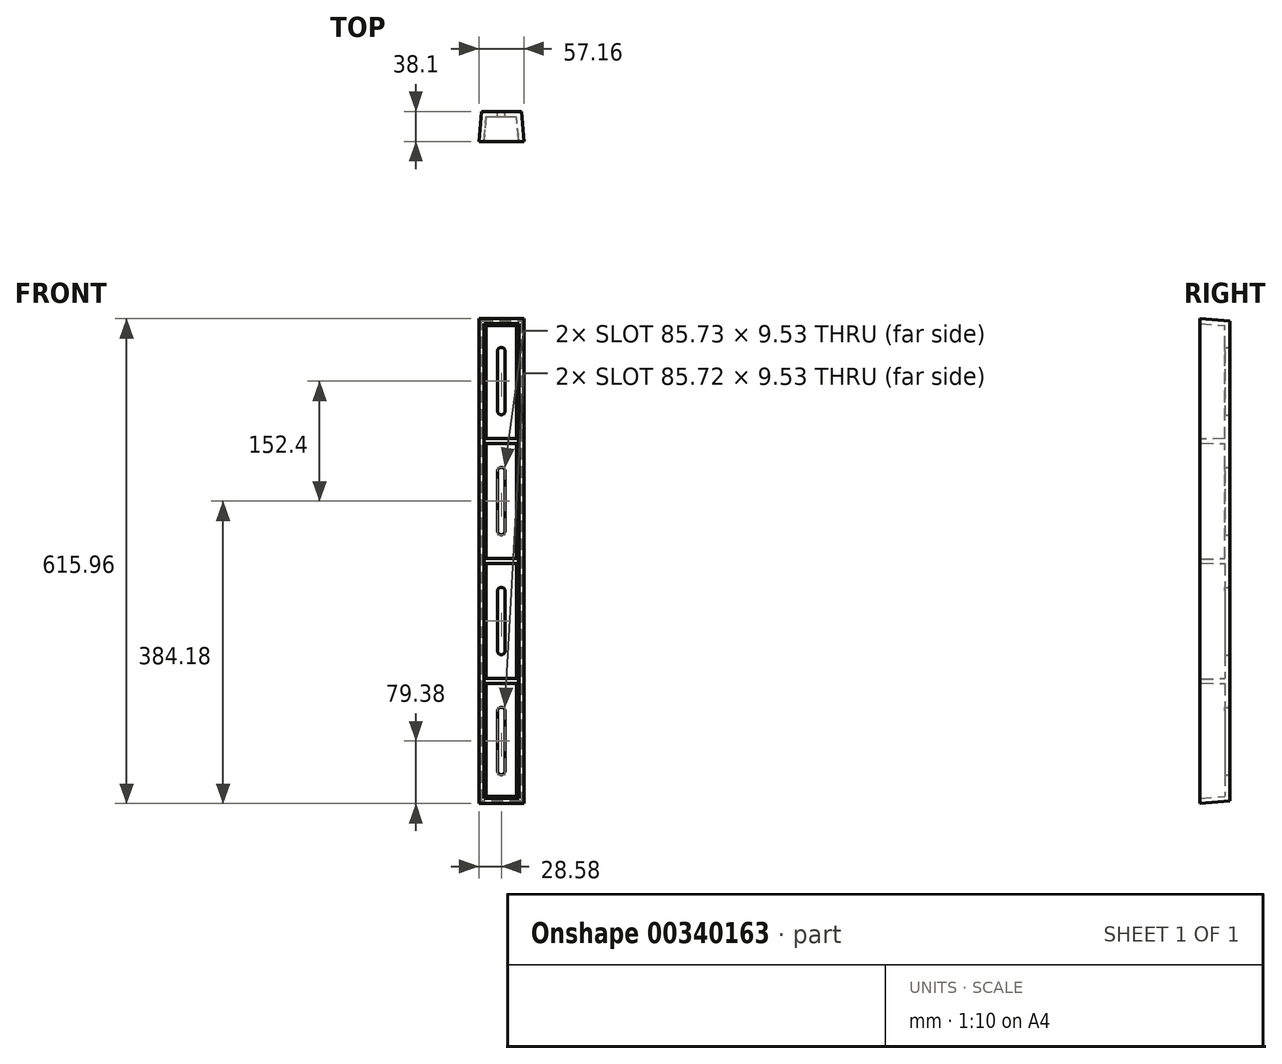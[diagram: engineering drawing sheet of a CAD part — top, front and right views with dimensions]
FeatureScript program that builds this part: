
annotation { "Feature Type Name" : "Feature", "Feature Type Description" : "" }
export const myFeature = defineFeature(function(context is Context, id is Id, definition is map)
    precondition{}
    {
        {
            var Q0;
            Q0=qCreatedBy(makeId("Front.planeOp"),FACE);
            var sketch = newSketch(context, id + "F0", { "sketchPlane" : qUnion([Q0])});
            skLineSegment(sketch, "E0.bottom", {"start": v(0, 0) * mm, "end": v(50.8, 0) * mm});
            skLineSegment(sketch, "E0.top", {"start": v(0, 609.6) * mm, "end": v(50.8, 609.6) * mm});
            skLineSegment(sketch, "E0.left", {"start": v(0, 0) * mm, "end": v(0, 609.6) * mm});
            skLineSegment(sketch, "E0.right", {"start": v(50.8, 0) * mm, "end": v(50.8, 609.6) * mm});
            skSolve(sketch);
        }
        {
            var Q0;
            Q0 = qSketchRegion(id + "F0", true);
            extrude(context, id + "F1", {"entities" : qUnion([Q0]), "depth" : 38.1 * mm, "hasDraft" : true, "draftAngle" : 4.76 * degree});
        }
        {
            var Q0;
            Q0=makeQuery(id+"F1.opExtrude","CAP_FACE",FACE,{"disambiguationData":[OSD([sQuery(id+"F0.wireOp",EDGE,"E0.bottom"),sQuery(id+"F0.wireOp",EDGE,"E0.top"),sQuery(id+"F0.wireOp",EDGE,"E0.left"),sQuery(id+"F0.wireOp",EDGE,"E0.right")])],"isStart":false});
            shell(context, id + "F2", {"entities" : qUnion([Q0]), "thickness" : 6.35 * mm});
        }
        {
            var Q0;
            Q0=makeQuery(id+"F1.opExtrude","CAP_FACE",FACE,{"disambiguationData":[OSD([sQuery(id+"F0.wireOp",EDGE,"E0.bottom"),sQuery(id+"F0.wireOp",EDGE,"E0.top"),sQuery(id+"F0.wireOp",EDGE,"E0.left"),sQuery(id+"F0.wireOp",EDGE,"E0.right")])],"isStart":true});
            var sketch = newSketch(context, id + "F3", { "sketchPlane" : qUnion([Q0])});
            skLineSegment(sketch, "E1", {"start": v(-25.4, 0) * mm, "end": v(-25.4, 152.4) * mm, "construction": true});
            skLineSegment(sketch, "E2", {"start": v(-25.4, 152.4) * mm, "end": v(-25.4, 304.8) * mm, "construction": true});
            skLineSegment(sketch, "E3", {"start": v(-25.4, 304.8) * mm, "end": v(-25.4, 457.2) * mm, "construction": true});
            skLineSegment(sketch, "E4", {"start": v(-25.4, 457.2) * mm, "end": v(-25.4, 609.6) * mm, "construction": true});
            skSolve(sketch);
        }
        {
            var Q0;
            Q0=makeQuery(id+"F1.opExtrude","CAP_EDGE",EDGE,{"disambiguationData":[OSD([sQuery(id+"F0.wireOp",EDGE,"E0.bottom")])],"isStart":true});
            cPoint(context, id + "F4", {"entities" : qUnion([Q0]), "parameter" : 0.5});
        }
        {
            var Q0;
            Q0=makeQuery(id+"F1.opExtrude","CAP_EDGE",EDGE,{"disambiguationData":[OSD([sQuery(id+"F0.wireOp",EDGE,"E0.bottom")])],"isStart":false});
            cPoint(context, id + "F5", {"entities" : qUnion([Q0]), "parameter" : 0.5});
        }
        {
            var Q0;
            {var subQ0=sQuery(id+"F0.wireOp",EDGE,"E0.top");Q0=makeQuery(id+"F2.opShell","OFFSET_EDGE",EDGE,{"disambiguationData":[OSD([subQ0]),TDD([makeQuery(id+"F1.opExtrude","CAP_EDGE",EDGE,{"disambiguationData":[OSD([subQ0])],"isStart":false})])]});}
            cPoint(context, id + "F6", {"entities" : qUnion([Q0]), "parameter" : 0.5});
        }
        {
            var Q0;
            Q0 = qCreatedBy(id + "F4" ,VERTEX);
            var Q1;
            Q1 = qCreatedBy(id + "F5" ,VERTEX);
            var Q2;
            Q2 = qCreatedBy(id + "F6" ,VERTEX);
            cPlane(context, id + "F7", {"entities" : qUnion([Q0, Q1, Q2]), "cplaneType" : CPlaneType.THREE_POINT, "offset" : 25.4 * mm, "width" : 152.4 * mm, "height" : 152.4 * mm});
        }
        {
            var Q0;
            Q0=qCreatedBy(id+"F7.planeOp",FACE);
            var sketch = newSketch(context, id + "F8", { "sketchPlane" : qUnion([Q0])});
            skLineSegment(sketch, "E5", {"start": v(-6.35, 603.76) * mm, "end": v(-6.35, 5.84) * mm});
            skLineSegment(sketch, "E6.0", {"start": v(0, 152.4) * mm, "end": v(0, 304.8) * mm, "construction": true});
            skLineSegment(sketch, "E7.0", {"start": v(0, 0) * mm, "end": v(0, 152.4) * mm});
            skLineSegment(sketch, "E8.0", {"start": v(0, 304.8) * mm, "end": v(0, 457.2) * mm, "construction": true});
            skLineSegment(sketch, "E9.0", {"start": v(0, 457.2) * mm, "end": v(0, 609.6) * mm, "construction": true});
            skLineSegment(sketch, "E10.0.0", {"start": v(-6.35, 5.84) * mm, "end": v(-6.35, 603.76) * mm});
            skLineSegment(sketch, "E10.0.1", {"start": v(-6.35, 603.76) * mm, "end": v(-38.1, 606.4) * mm});
            skLineSegment(sketch, "E10.0.2", {"start": v(-38.1, 606.4) * mm, "end": v(-38.1, 3.2) * mm, "construction": true});
            skLineSegment(sketch, "E10.0.3", {"start": v(-38.1, 3.2) * mm, "end": v(-6.35, 5.84) * mm});
            skLineSegment(sketch, "E11", {"start": v(0, 152.4) * mm, "end": v(-38.1, 152.4) * mm, "construction": true});
            skLineSegment(sketch, "E12", {"start": v(0, 304.8) * mm, "end": v(-38.1, 304.8) * mm, "construction": true});
            skLineSegment(sketch, "E13", {"start": v(0, 457.2) * mm, "end": v(-38.1, 457.2) * mm, "construction": true});
            skLineSegment(sketch, "E14.0", {"start": v(0, 155.58) * mm, "end": v(-6.35, 155.58) * mm, "construction": true});
            skLineSegment(sketch, "E15.0", {"start": v(0, 149.22) * mm, "end": v(-6.35, 149.22) * mm, "construction": true});
            skLineSegment(sketch, "E16.0", {"start": v(0, 301.63) * mm, "end": v(-6.35, 301.63) * mm, "construction": true});
            skLineSegment(sketch, "E17.0", {"start": v(0, 307.98) * mm, "end": v(-6.35, 307.98) * mm, "construction": true});
            skLineSegment(sketch, "E18.0", {"start": v(0, 460.38) * mm, "end": v(-6.35, 460.38) * mm, "construction": true});
            skLineSegment(sketch, "E19.0", {"start": v(0, 454.03) * mm, "end": v(-6.35, 454.03) * mm, "construction": true});
            skArc(sketch, "E20", {"start": v(-35.78, 154.78) * mm, "mid": v(-38.1, 152.4) * mm, "end": v(-35.78, 150.02) * mm});
            skArc(sketch, "E21", {"start": v(-35.78, 307.18) * mm, "mid": v(-38.1, 304.8) * mm, "end": v(-35.78, 302.42) * mm});
            skArc(sketch, "E22", {"start": v(-35.78, 459.58) * mm, "mid": v(-38.1, 457.2) * mm, "end": v(-35.78, 454.82) * mm});
            skLineSegment(sketch, "E23", {"start": v(-6.35, 149.22) * mm, "end": v(-35.78, 150.02) * mm});
            skLineSegment(sketch, "E24", {"start": v(-6.35, 155.57) * mm, "end": v(-35.78, 154.78) * mm});
            skLineSegment(sketch, "E25", {"start": v(-6.35, 301.63) * mm, "end": v(-35.78, 302.42) * mm});
            skLineSegment(sketch, "E26", {"start": v(-6.35, 307.98) * mm, "end": v(-35.78, 307.18) * mm});
            skLineSegment(sketch, "E27", {"start": v(-6.35, 454.03) * mm, "end": v(-35.78, 454.82) * mm});
            skLineSegment(sketch, "E28", {"start": v(-6.35, 460.38) * mm, "end": v(-35.78, 459.58) * mm});
            skSolve(sketch);
        }
        {
            var Q0;
            Q0 = qSketchRegion(id + "F8", true);
            var Q1;
            Q1=makeQuery(id+"F2.opShell","OFFSET_FACE",FACE,{"disambiguationData":[OSD([sQuery(id+"F0.wireOp",EDGE,"E0.left")])]});
            var Q2;
            Q2=makeQuery(id+"F2.opShell","OFFSET_FACE",FACE,{"disambiguationData":[OSD([sQuery(id+"F0.wireOp",EDGE,"E0.right")])]});
            extrude(context, id + "F9", {"entities" : qUnion([Q0]), "operationType" : NewBodyOperationType.ADD, "endBound" : BoundingType.UP_TO_SURFACE, "oppositeDirection" : true, "endBoundEntityFace" : qUnion([Q1]), "depth" : 25.4 * mm, "hasSecondDirection" : true, "secondDirectionBound" : BoundingType.UP_TO_SURFACE, "secondDirectionOppositeDirection" : false, "secondDirectionBoundEntityFace" : qUnion([Q2]), "secondDirectionDepth" : 25.4 * mm});
        }
        {
            var Q0;
            Q0=makeQuery(id+"F3.imprint","IMPRINT",FACE,{"disambiguationData":[TD([[makeQuery(id+"F3.imprint","IMPRINT",EDGE,{"derivedFrom":makeQuery(id+"F1.opExtrude","CAP_EDGE",EDGE,{"disambiguationData":[OSD([sQuery(id+"F0.wireOp",EDGE,"E0.bottom")])],"isStart":true})}),-1.0]])]});
            var sketch = newSketch(context, id + "F10", { "sketchPlane" : qUnion([Q0])});
            skLineSegment(sketch, "E29.0", {"start": v(-25.4, 457.2) * mm, "end": v(-25.4, 609.6) * mm, "construction": true});
            skLineSegment(sketch, "E30.0", {"start": v(-25.4, 304.8) * mm, "end": v(-25.4, 457.2) * mm, "construction": true});
            skLineSegment(sketch, "E31.0", {"start": v(-25.4, 152.4) * mm, "end": v(-25.4, 304.8) * mm, "construction": true});
            skLineSegment(sketch, "E32.0", {"start": v(-25.4, 0) * mm, "end": v(-25.4, 152.4) * mm, "construction": true});
            skLineSegment(sketch, "E33.bottom", {"start": v(-30.16, 495.3) * mm, "end": v(-20.64, 495.3) * mm});
            skLineSegment(sketch, "E33.top", {"start": v(-30.16, 571.5) * mm, "end": v(-20.64, 571.5) * mm});
            skLineSegment(sketch, "E33.left", {"start": v(-30.16, 495.3) * mm, "end": v(-30.16, 571.5) * mm});
            skLineSegment(sketch, "E33.right", {"start": v(-20.64, 495.3) * mm, "end": v(-20.64, 571.5) * mm});
            skPoint(sketch, "E33.middle", {"position": v(-25.4, 533.4) * mm});
            skLineSegment(sketch, "E34.bottom", {"start": v(-30.16, 342.9) * mm, "end": v(-20.64, 342.9) * mm});
            skLineSegment(sketch, "E34.top", {"start": v(-30.16, 419.1) * mm, "end": v(-20.64, 419.1) * mm});
            skLineSegment(sketch, "E34.left", {"start": v(-30.16, 342.9) * mm, "end": v(-30.16, 419.1) * mm});
            skLineSegment(sketch, "E34.right", {"start": v(-20.64, 342.9) * mm, "end": v(-20.64, 419.1) * mm});
            skPoint(sketch, "E34.middle", {"position": v(-25.4, 381) * mm});
            skLineSegment(sketch, "E35.bottom", {"start": v(-30.16, 190.5) * mm, "end": v(-20.64, 190.5) * mm});
            skLineSegment(sketch, "E35.top", {"start": v(-30.16, 266.7) * mm, "end": v(-20.64, 266.7) * mm});
            skLineSegment(sketch, "E35.left", {"start": v(-30.16, 190.5) * mm, "end": v(-30.16, 266.7) * mm});
            skLineSegment(sketch, "E35.right", {"start": v(-20.64, 190.5) * mm, "end": v(-20.64, 266.7) * mm});
            skPoint(sketch, "E35.middle", {"position": v(-25.4, 228.6) * mm});
            skLineSegment(sketch, "E36.bottom", {"start": v(-30.16, 38.1) * mm, "end": v(-20.64, 38.1) * mm});
            skLineSegment(sketch, "E36.top", {"start": v(-30.16, 114.3) * mm, "end": v(-20.64, 114.3) * mm});
            skLineSegment(sketch, "E36.left", {"start": v(-30.16, 38.1) * mm, "end": v(-30.16, 114.3) * mm});
            skLineSegment(sketch, "E36.right", {"start": v(-20.64, 38.1) * mm, "end": v(-20.64, 114.3) * mm});
            skPoint(sketch, "E36.middle", {"position": v(-25.4, 76.2) * mm});
            skCircle(sketch, "E37", {"center": v(-25.4, 571.5) * mm, "radius": 4.76 * mm});
            skCircle(sketch, "E38", {"center": v(-25.4, 495.3) * mm, "radius": 4.76 * mm});
            skCircle(sketch, "E39", {"center": v(-25.4, 419.1) * mm, "radius": 4.76 * mm});
            skCircle(sketch, "E40", {"center": v(-25.4, 266.7) * mm, "radius": 4.76 * mm});
            skCircle(sketch, "E41", {"center": v(-25.4, 190.5) * mm, "radius": 4.76 * mm});
            skCircle(sketch, "E42", {"center": v(-25.4, 114.3) * mm, "radius": 4.76 * mm});
            skCircle(sketch, "E43", {"center": v(-25.4, 38.1) * mm, "radius": 4.76 * mm});
            skCircle(sketch, "E44", {"center": v(-25.4, 342.9) * mm, "radius": 4.76 * mm});
            skSolve(sketch);
        }
        {
            var Q0;
            Q0 = qSketchRegion(id + "F10", true);
            extrude(context, id + "F11", {"entities" : qUnion([Q0]), "operationType" : NewBodyOperationType.REMOVE, "endBound" : BoundingType.THROUGH_ALL, "oppositeDirection" : true, "depth" : 25.4 * mm});
        }
    });
